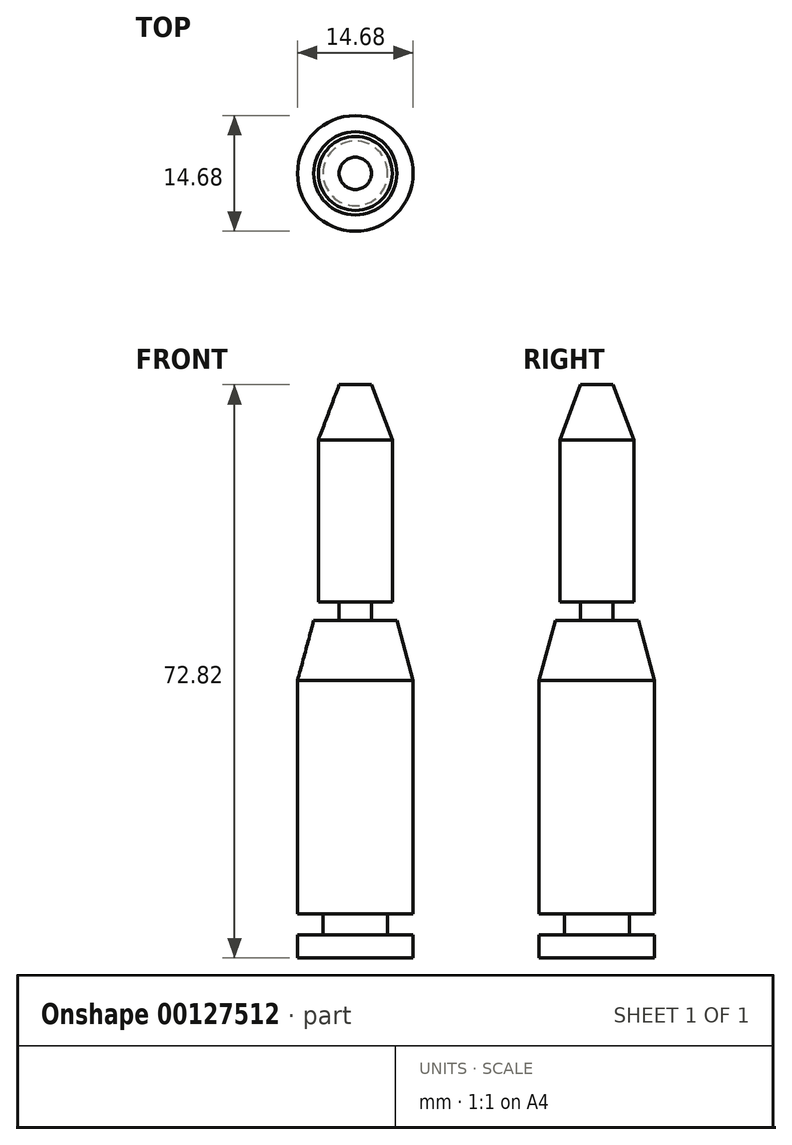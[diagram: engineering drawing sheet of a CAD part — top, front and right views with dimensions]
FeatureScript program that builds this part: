
annotation { "Feature Type Name" : "Feature", "Feature Type Description" : "" }
export const myFeature = defineFeature(function(context is Context, id is Id, definition is map)
    precondition{}
    {
        {
            var Q0;
            Q0=qCreatedBy(makeId("Front.planeOp"),FACE);
            var sketch = newSketch(context, id + "F0", { "sketchPlane" : qUnion([Q0])});
            skLineSegment(sketch, "E0", {"start": v(0, 40.96) * mm, "end": v(2.06, 40.96) * mm});
            skLineSegment(sketch, "E1", {"start": v(2.06, 40.96) * mm, "end": v(4.7, 33.91) * mm});
            skLineSegment(sketch, "E2", {"start": v(4.7, 33.91) * mm, "end": v(4.7, 13.36) * mm});
            skLineSegment(sketch, "E3", {"start": v(4.7, 13.36) * mm, "end": v(2.06, 13.36) * mm});
            skLineSegment(sketch, "E4", {"start": v(2.06, 13.36) * mm, "end": v(2.06, 11.01) * mm});
            skLineSegment(sketch, "E5", {"start": v(2.06, 11.01) * mm, "end": v(5.29, 11.01) * mm});
            skLineSegment(sketch, "E6", {"start": v(5.29, 11.01) * mm, "end": v(7.34, 3.38) * mm});
            skLineSegment(sketch, "E7", {"start": v(7.34, 3.38) * mm, "end": v(7.34, -26.28) * mm});
            skLineSegment(sketch, "E8", {"start": v(7.34, -26.28) * mm, "end": v(4.11, -26.28) * mm});
            skLineSegment(sketch, "E9", {"start": v(4.11, -26.28) * mm, "end": v(4.11, -28.92) * mm});
            skLineSegment(sketch, "E10", {"start": v(4.11, -28.92) * mm, "end": v(7.34, -28.92) * mm});
            skLineSegment(sketch, "E11", {"start": v(7.34, -28.92) * mm, "end": v(7.34, -31.86) * mm});
            skLineSegment(sketch, "E12", {"start": v(7.34, -31.86) * mm, "end": v(0, -31.86) * mm});
            skLineSegment(sketch, "E13", {"start": v(0, -31.86) * mm, "end": v(0, 40.96) * mm});
            skSolve(sketch);
        }
        {
            var Q0;
            Q0=makeQuery(id+"F0.imprint","IMPRINT",FACE,{"disambiguationData":[TD([[makeQuery(id+"F0.imprint","IMPRINT",EDGE,{"derivedFrom":sQuery(id+"F0.wireOp",EDGE,"E0")}),-1.0]])]});
            var Q1;
            Q1=sQuery(id+"F0.wireOp",EDGE,"E13");
            revolve(context, id + "F1", {"entities" : qUnion([Q0]), "axis" : qUnion([Q1]), "revolveType" : RevolveType.FULL});
        }
    });
